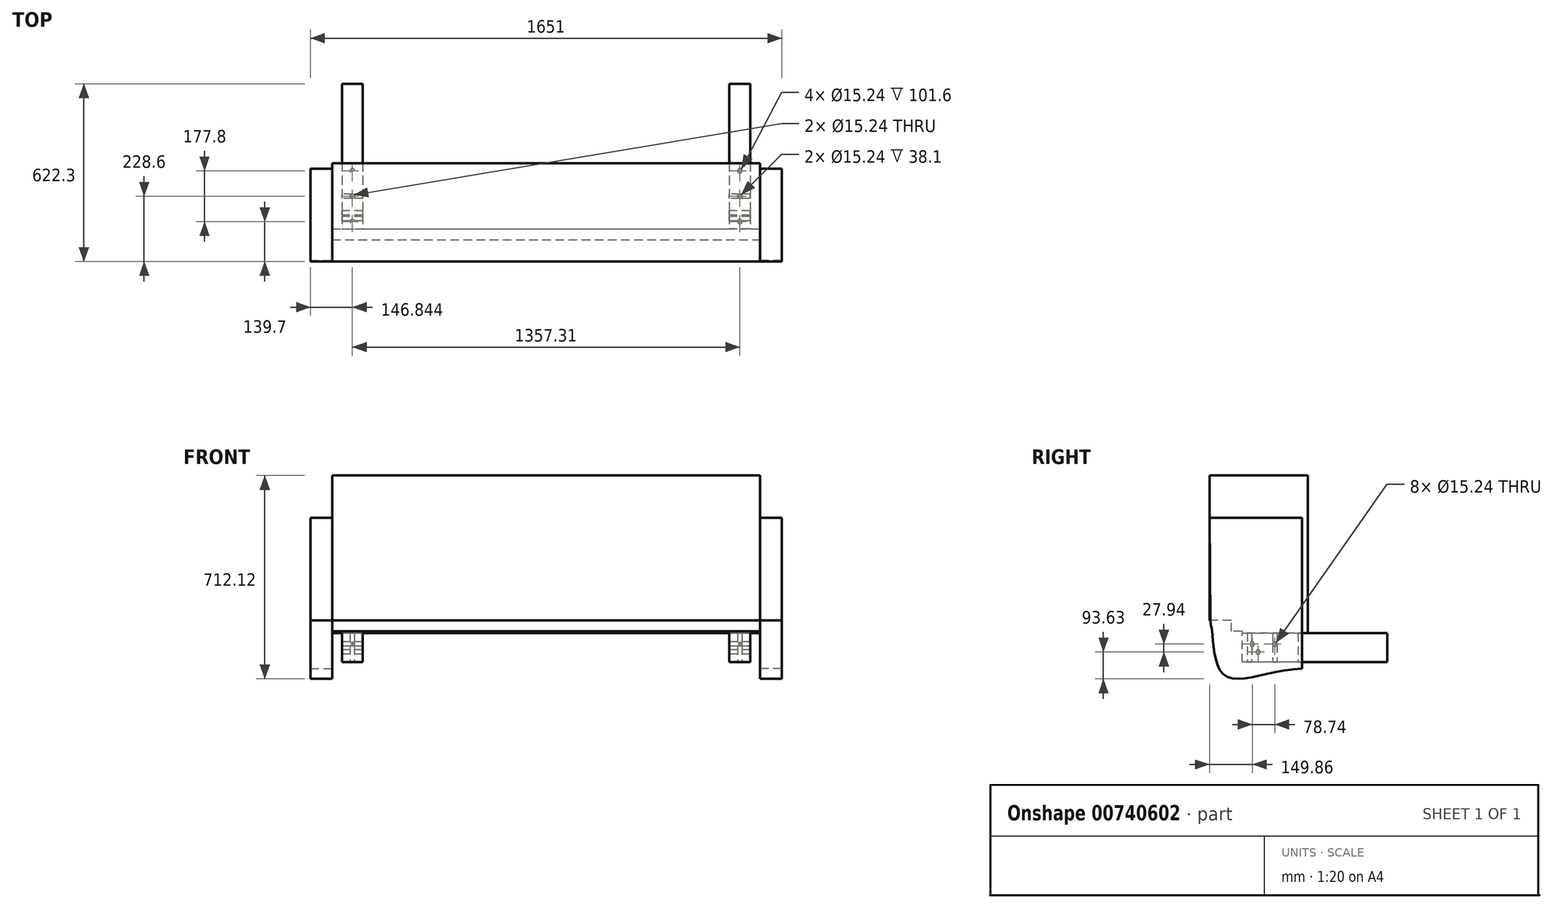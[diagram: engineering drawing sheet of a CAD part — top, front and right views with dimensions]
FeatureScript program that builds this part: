
annotation { "Feature Type Name" : "Feature", "Feature Type Description" : "" }
export const myFeature = defineFeature(function(context is Context, id is Id, definition is map)
    precondition{}
    {
        {
            var Q0;
            Q0=qCreatedBy(makeId("Front.planeOp"),FACE);
            var sketch = newSketch(context, id + "F0", { "sketchPlane" : qUnion([Q0])});
            skLineSegment(sketch, "E0", {"start": v(0, 0) * mm, "end": v(-715.17, 0) * mm, "construction": true});
            skLineSegment(sketch, "E1", {"start": v(0, 0) * mm, "end": v(715.17, 0) * mm, "construction": true});
            skLineSegment(sketch, "E2.bottom", {"start": v(-715.17, 0) * mm, "end": v(-642.14, 0) * mm});
            skLineSegment(sketch, "E2.top", {"start": v(-715.17, 101.6) * mm, "end": v(-642.14, 101.6) * mm});
            skLineSegment(sketch, "E2.left", {"start": v(-715.17, 0) * mm, "end": v(-715.17, 101.6) * mm});
            skLineSegment(sketch, "E2.right", {"start": v(-642.14, 0) * mm, "end": v(-642.14, 101.6) * mm});
            skLineSegment(sketch, "E3.bottom", {"start": v(715.17, 0) * mm, "end": v(642.14, 0) * mm});
            skLineSegment(sketch, "E3.top", {"start": v(715.17, 101.6) * mm, "end": v(642.14, 101.6) * mm});
            skLineSegment(sketch, "E3.left", {"start": v(715.17, 0) * mm, "end": v(715.17, 101.6) * mm});
            skLineSegment(sketch, "E3.right", {"start": v(642.14, 0) * mm, "end": v(642.14, 101.6) * mm});
            skSolve(sketch);
        }
        {
            var Q0;
            Q0=makeQuery(id+"F0.imprint","IMPRINT",FACE,{"disambiguationData":[TD([[makeQuery(id+"F0.imprint","IMPRINT",EDGE,{"derivedFrom":sQuery(id+"F0.wireOp",EDGE,"E2.bottom")}),1.0]])]});
            var Q1;
            Q1=makeQuery(id+"F0.imprint","IMPRINT",FACE,{"disambiguationData":[TD([[makeQuery(id+"F0.imprint","IMPRINT",EDGE,{"derivedFrom":sQuery(id+"F0.wireOp",EDGE,"E3.bottom")}),-1.0]])]});
            extrude(context, id + "F1", {"entities" : qUnion([Q0, Q1]), "oppositeDirection" : true, "depth" : 508 * mm, "offsetDistance" : 25.4 * mm});
        }
        {
            var Q0;
            Q0=makeQuery(id+"F1.opExtrude","SWEPT_FACE",FACE,{"disambiguationData":[OSD([sQuery(id+"F0.wireOp",EDGE,"E2.bottom")])]});
            var sketch = newSketch(context, id + "F2", { "sketchPlane" : qUnion([Q0])});
            skCircle(sketch, "E4", {"center": v(-678.66, -25.4) * mm, "radius": 7.62 * mm});
            skCircle(sketch, "E5", {"center": v(-678.66, -114.3) * mm, "radius": 7.62 * mm});
            skCircle(sketch, "E6", {"center": v(-678.66, -203.2) * mm, "radius": 7.62 * mm});
            skCircle(sketch, "E7", {"center": v(678.66, -25.4) * mm, "radius": 7.62 * mm});
            skCircle(sketch, "E8", {"center": v(678.66, -114.3) * mm, "radius": 7.62 * mm});
            skCircle(sketch, "E9", {"center": v(678.66, -203.2) * mm, "radius": 7.62 * mm});
            skSolve(sketch);
        }
        {
            var Q0;
            Q0 = qSketchRegion(id + "F2", true);
            extrude(context, id + "F3", {"entities" : qUnion([Q0]), "operationType" : NewBodyOperationType.REMOVE, "endBound" : BoundingType.THROUGH_ALL, "oppositeDirection" : true, "depth" : 25.4 * mm, "offsetDistance" : 25.4 * mm});
        }
        {
            var Q0;
            Q0=makeQuery(id+"F1.opExtrude","SWEPT_FACE",FACE,{"disambiguationData":[OSD([sQuery(id+"F0.wireOp",EDGE,"E2.left")])]});
            var sketch = newSketch(context, id + "F4", { "sketchPlane" : qUnion([Q0])});
            skCircle(sketch, "E10", {"center": v(-35.56, 63.5) * mm, "radius": 7.62 * mm});
            skCircle(sketch, "E11", {"center": v(-55.88, 35.56) * mm, "radius": 7.62 * mm});
            skCircle(sketch, "E12", {"center": v(-114.3, 63.5) * mm, "radius": 7.62 * mm});
            skLineSegment(sketch, "E13.0", {"start": v(-106.68, 0) * mm, "end": v(-121.92, 0) * mm});
            skSolve(sketch);
        }
        {
            var Q0;
            Q0=makeQuery(id+"F4.imprint","IMPRINT",FACE,{"disambiguationData":[TD([[makeQuery(id+"F4.imprint","IMPRINT",EDGE,{"derivedFrom":sQuery(id+"F4.wireOp",EDGE,"E12")}),1.0]])]});
            var Q1;
            Q1=makeQuery(id+"F4.imprint","IMPRINT",FACE,{"disambiguationData":[TD([[makeQuery(id+"F4.imprint","IMPRINT",EDGE,{"derivedFrom":sQuery(id+"F4.wireOp",EDGE,"E11")}),1.0]])]});
            var Q2;
            Q2=makeQuery(id+"F4.imprint","IMPRINT",FACE,{"disambiguationData":[TD([[makeQuery(id+"F4.imprint","IMPRINT",EDGE,{"derivedFrom":sQuery(id+"F4.wireOp",EDGE,"E10")}),1.0]])]});
            extrude(context, id + "F5", {"entities" : qUnion([Q0, Q1, Q2]), "operationType" : NewBodyOperationType.REMOVE, "endBound" : BoundingType.THROUGH_ALL, "oppositeDirection" : true, "depth" : 25.4 * mm, "offsetDistance" : 25.4 * mm});
        }
        {
            var Q0;
            Q0=qCreatedBy(makeId("Right.planeOp"),FACE);
            cPlane(context, id + "F6", {"entities" : qUnion([Q0]), "cplaneType" : CPlaneType.OFFSET, "offset" : 749.3 * mm, "width" : 152.4 * mm, "height" : 152.4 * mm});
        }
        {
            var Q0;
            Q0=qCreatedBy(id+"F6.planeOp",FACE);
            var sketch = newSketch(context, id + "F7", { "sketchPlane" : qUnion([Q0])});
            skLineSegment(sketch, "E14.0", {"start": v(508, 0) * mm, "end": v(0, 0) * mm});
            skLineSegment(sketch, "E15.0", {"start": v(0, 0) * mm, "end": v(0, 101.6) * mm});
            skLineSegment(sketch, "E16", {"start": v(0, 0) * mm, "end": v(0, 107.95) * mm, "construction": true});
            skLineSegment(sketch, "E17", {"start": v(0, 107.95) * mm, "end": v(-38.1, 107.95) * mm, "construction": true});
            skLineSegment(sketch, "E18", {"start": v(-38.1, 107.95) * mm, "end": v(-38.1, 146.05) * mm, "construction": true});
            skLineSegment(sketch, "E19", {"start": v(-38.1, 146.05) * mm, "end": v(-114.3, 146.05) * mm, "construction": true});
            skLineSegment(sketch, "E20", {"start": v(0, 101.6) * mm, "end": v(0, 107.95) * mm, "construction": true});
            skLineSegment(sketch, "E21", {"start": v(0, 107.95) * mm, "end": v(-38.1, 107.95) * mm});
            skLineSegment(sketch, "E22", {"start": v(-38.1, 107.95) * mm, "end": v(-38.1, 146.05) * mm});
            skLineSegment(sketch, "E23", {"start": v(-38.1, 146.05) * mm, "end": v(-114.3, 146.05) * mm});
            skLineSegment(sketch, "E24", {"start": v(-114.3, 146.05) * mm, "end": v(-114.3, 654.05) * mm});
            skLineSegment(sketch, "E25", {"start": v(0, 107.95) * mm, "end": v(0, 101.6) * mm});
            skLineSegment(sketch, "E26", {"start": v(0, 101.6) * mm, "end": v(229.9, 101.6) * mm});
            skLineSegment(sketch, "E27", {"start": v(229.9, 101.6) * mm, "end": v(229.9, 654.05) * mm});
            skLineSegment(sketch, "E28", {"start": v(229.9, 654.05) * mm, "end": v(-114.3, 654.05) * mm});
            skSolve(sketch);
        }
        {
            var Q0;
            Q0=makeQuery(id+"F7.imprint","IMPRINT",FACE,{"disambiguationData":[TD([[makeQuery(id+"F7.imprint","IMPRINT",EDGE,{"derivedFrom":sQuery(id+"F7.wireOp",EDGE,"E21")}),-1.0]])]});
            extrude(context, id + "F8", {"entities" : qUnion([Q0]), "operationType" : NewBodyOperationType.ADD, "oppositeDirection" : true, "depth" : 1498.6 * mm, "offsetDistance" : 25.4 * mm});
        }
        {
            var Q0;
            Q0=makeQuery(id+"F8.opExtrude","CAP_FACE",FACE,{"disambiguationData":[OSD([sQuery(id+"F7.wireOp",EDGE,"E21"),sQuery(id+"F7.wireOp",EDGE,"E22"),sQuery(id+"F7.wireOp",EDGE,"E23"),sQuery(id+"F7.wireOp",EDGE,"E24"),sQuery(id+"F7.wireOp",EDGE,"E25"),sQuery(id+"F7.wireOp",EDGE,"E26"),sQuery(id+"F7.wireOp",EDGE,"E27"),sQuery(id+"F7.wireOp",EDGE,"E28")])],"isStart":true});
            var sketch = newSketch(context, id + "F9", { "sketchPlane" : qUnion([Q0])});
            skLineSegment(sketch, "E29", {"start": v(-38.1, 107.95) * mm, "end": v(-38.1, -44.45) * mm, "construction": true});
            skLineSegment(sketch, "E30", {"start": v(-38.1, -44.45) * mm, "end": v(-63.5, -44.45) * mm, "construction": true});
            skLineSegment(sketch, "E31", {"start": v(-38.1, 107.95) * mm, "end": v(-104.78, 107.95) * mm, "construction": true});
            skLineSegment(sketch, "E32", {"start": v(-38.1, 146.05) * mm, "end": v(-111.13, 146.05) * mm, "construction": true});
            skLineSegment(sketch, "E33", {"start": v(-38.1, -44.45) * mm, "end": v(210.2, -22.53) * mm, "construction": true});
            skFitSpline(sketch, "E34", {"points": [v(-111.12, 146.05) * mm, v(-104.78, 107.95) * mm, v(-63.5, -44.45) * mm, v(210.2, -22.53) * mm], "startDerivative": vector(16.83, -308.24) * mm, "endDerivative": vector(697.94, 7.27) * mm});
            skLineSegment(sketch, "E35", {"start": v(210.2, -22.53) * mm, "end": v(210.2, 506.17) * mm});
            skLineSegment(sketch, "E36", {"start": v(210.2, 506.17) * mm, "end": v(-114.3, 506.17) * mm});
            skLineSegment(sketch, "E37", {"start": v(-114.3, 506.17) * mm, "end": v(-111.13, 146.05) * mm});
            skSolve(sketch);
        }
        {
            var Q0;
            {var subQ5=sQuery(id+"F9.wireOp",EDGE,"E36");Q0=makeQuery(id+"F9.imprint","IMPRINT",FACE,{"disambiguationData":[TD([[makeQuery(id+"F9.imprint","IMPRINT",EDGE,{"derivedFrom":subQ5}),1.0]])]});}
            var Q1;
            {var subQ2=sQuery(id+"F9.wireOp",EDGE,"E34");Q1=makeQuery(id+"F9.imprint","IMPRINT",FACE,{"disambiguationData":[TD([[makeQuery(id+"F9.imprint","IMPRINT",EDGE,{"derivedFrom":subQ2}),1.0]])]});}
            extrude(context, id + "F10", {"entities" : qUnion([Q0, Q1]), "depth" : 76.2 * mm, "offsetDistance" : 25.4 * mm});
        }
        {
            var Q0;
            Q0=makeQuery(id+"F10.opExtrude","SWEPT_BODY",BODY,{"disambiguationData":[OSD([sQuery(id+"F9.wireOp",EDGE,"E34"),sQuery(id+"F9.wireOp",EDGE,"E35"),sQuery(id+"F9.wireOp",EDGE,"E36"),sQuery(id+"F9.wireOp",EDGE,"E37")])]});
            var Q1;
            Q1=qCreatedBy(makeId("Right.planeOp"),FACE);
            mirror(context, id + "F11", {"operationType" : NewBodyOperationType.ADD, "entities" : qUnion([Q0]), "mirrorPlane" : qUnion([Q1])});
        }
    });
